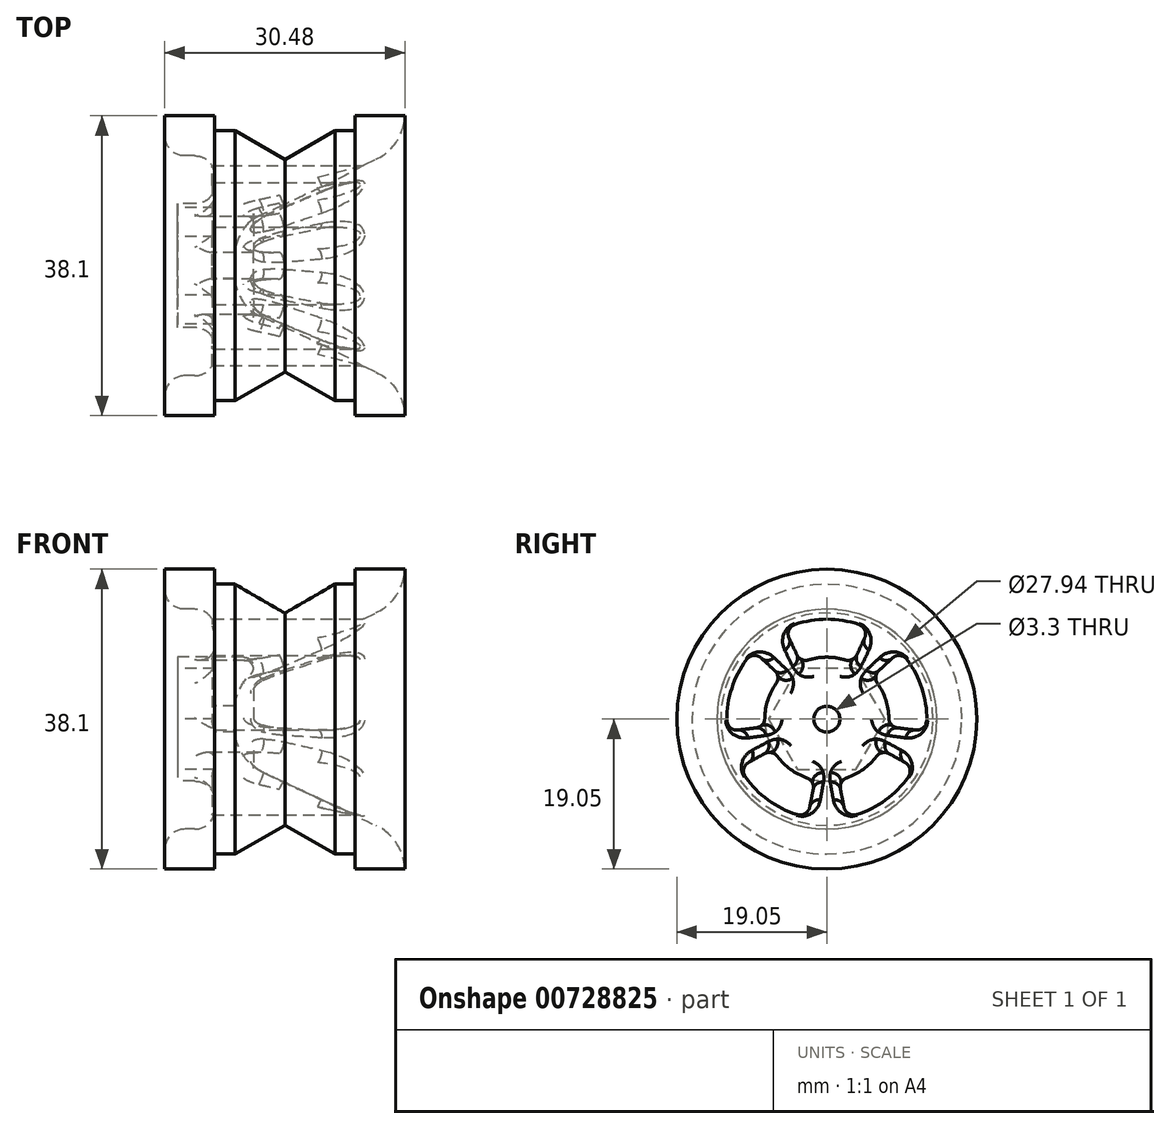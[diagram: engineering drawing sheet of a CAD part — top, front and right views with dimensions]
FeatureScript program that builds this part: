
annotation { "Feature Type Name" : "Feature", "Feature Type Description" : "" }
export const myFeature = defineFeature(function(context is Context, id is Id, definition is map)
    precondition{}
    {
        {
            var Q0;
            Q0=qCreatedBy(makeId("Front.planeOp"),FACE);
            var sketch = newSketch(context, id + "F0", { "sketchPlane" : qUnion([Q0])});
            skLineSegment(sketch, "E0", {"start": v(0, 0) * mm, "end": v(0, 50.34) * mm, "construction": true});
            skLineSegment(sketch, "E1", {"start": v(6.35, 17.15) * mm, "end": v(8.9, 17.15) * mm});
            skLineSegment(sketch, "E2", {"start": v(8.9, 17.15) * mm, "end": v(8.9, 19.05) * mm});
            skLineSegment(sketch, "E3", {"start": v(8.9, 19.05) * mm, "end": v(15.24, 19.05) * mm});
            skLineSegment(sketch, "E4", {"start": v(15.24, 19.05) * mm, "end": v(15.24, 15.24) * mm});
            skLineSegment(sketch, "E5", {"start": v(15.24, 15.24) * mm, "end": v(-6.35, 5.08) * mm});
            skLineSegment(sketch, "E6.MirrorCS", {"start": v(-8.9, 17.15) * mm, "end": v(-8.9, 19.05) * mm});
            skLineSegment(sketch, "E7.MirrorCS", {"start": v(-8.9, 19.05) * mm, "end": v(-15.24, 19.05) * mm});
            skLineSegment(sketch, "E8", {"start": v(-8.9, 7.87) * mm, "end": v(-8.9, 13.97) * mm});
            skLineSegment(sketch, "E9", {"start": v(-8.9, 13.97) * mm, "end": v(-15.24, 13.97) * mm});
            skLineSegment(sketch, "E10", {"start": v(-15.24, 19.05) * mm, "end": v(-15.24, 13.97) * mm});
            skLineSegment(sketch, "E11", {"start": v(-8.9, 7.87) * mm, "end": v(-13.59, 7.87) * mm});
            skLineSegment(sketch, "E12", {"start": v(-13.59, 7.87) * mm, "end": v(-13.59, 0) * mm});
            skLineSegment(sketch, "E13", {"start": v(-27.96, 0) * mm, "end": v(34.54, 0) * mm, "construction": true});
            skLineSegment(sketch, "E14", {"start": v(-6.35, 5.08) * mm, "end": v(-6.35, 0) * mm});
            skLineSegment(sketch, "E15", {"start": v(-13.59, 0) * mm, "end": v(-6.35, 0) * mm});
            skLineSegment(sketch, "E16", {"start": v(-8.9, 17.15) * mm, "end": v(-6.35, 17.15) * mm});
            skLineSegment(sketch, "E17", {"start": v(-6.35, 17.15) * mm, "end": v(0, 13.48) * mm});
            skLineSegment(sketch, "E18", {"start": v(0, 13.48) * mm, "end": v(6.35, 17.15) * mm});
            skSolve(sketch);
        }
        {
            var Q0;
            Q0 = qSketchRegion(id + "F0", true);
            var Q1;
            Q1=sQuery(id+"F0.wireOp",EDGE,"E13");
            revolve(context, id + "F1", {"surfaceOperationType" : NewSurfaceOperationType.NEW, "entities" : qUnion([Q0]), "axis" : qUnion([Q1]), "revolveType" : RevolveType.FULL});
        }
        {
            var Q0;
            Q0=makeQuery(id+"F1.opRevolve","SWEPT_FACE",FACE,{"disambiguationData":[OSD([sQuery(id+"F0.wireOp",EDGE,"E12")])]});
            var sketch = newSketch(context, id + "F2", { "sketchPlane" : qUnion([Q0])});
            skCircle(sketch, "E19.cCircle", {"center": v(0, 0) * mm, "radius": 6.41 * mm, "construction": true});
            skLineSegment(sketch, "E19.0", {"start": v(7.4, 0) * mm, "end": v(3.7, -6.41) * mm});
            skLineSegment(sketch, "E19.1", {"start": v(3.7, -6.41) * mm, "end": v(-3.7, -6.41) * mm});
            skLineSegment(sketch, "E19.2", {"start": v(-3.7, -6.41) * mm, "end": v(-7.4, 0) * mm});
            skLineSegment(sketch, "E19.3", {"start": v(-7.4, 0) * mm, "end": v(-3.7, 6.41) * mm});
            skLineSegment(sketch, "E19.4", {"start": v(-3.7, 6.41) * mm, "end": v(3.7, 6.41) * mm});
            skLineSegment(sketch, "E19.5", {"start": v(3.7, 6.41) * mm, "end": v(7.4, 0) * mm});
            skPoint(sketch, "E19.0.midPoint", {"position": v(5.55, -3.2) * mm});
            skSolve(sketch);
        }
        {
            var Q0;
            Q0 = qSketchRegion(id + "F2", true);
            var Q1;
            Q1=makeQuery(id+"F1.opRevolve","SWEPT_FACE",FACE,{"disambiguationData":[OSD([sQuery(id+"F0.wireOp",EDGE,"E8")])]});
            extrude(context, id + "F3", {"entities" : qUnion([Q0]), "operationType" : NewBodyOperationType.REMOVE, "endBound" : BoundingType.UP_TO_SURFACE, "oppositeDirection" : true, "depth" : 25.4 * mm, "endBoundEntityFace" : qUnion([Q1]), "offsetDistance" : 25.4 * mm});
        }
        {
            var Q0;
            Q0=makeQuery(id+"F3.boolean.opBoolean","COPY",FACE,{"derivedFrom":makeQuery(id+"F3.opExtrude","CAP_FACE",FACE,{"disambiguationData":[OSD([sQuery(id+"F2.wireOp",EDGE,"E19.0"),sQuery(id+"F2.wireOp",EDGE,"E19.1"),sQuery(id+"F2.wireOp",EDGE,"E19.2"),sQuery(id+"F2.wireOp",EDGE,"E19.3"),sQuery(id+"F2.wireOp",EDGE,"E19.4"),sQuery(id+"F2.wireOp",EDGE,"E19.5")])],"isStart":false})});
            var sketch = newSketch(context, id + "F4", { "sketchPlane" : qUnion([Q0])});
            skCircle(sketch, "E20", {"center": v(0, 0) * mm, "radius": 1.65 * mm});
            skSolve(sketch);
        }
        {
            var Q0;
            Q0 = qSketchRegion(id + "F4", true);
            extrude(context, id + "F5", {"entities" : qUnion([Q0]), "operationType" : NewBodyOperationType.REMOVE, "endBound" : BoundingType.THROUGH_ALL, "oppositeDirection" : true, "depth" : 25.4 * mm, "offsetDistance" : 25.4 * mm});
        }
        {
            var Q0;
            Q0=makeQuery(id+"F1.opRevolve","SWEPT_EDGE",EDGE,{"disambiguationData":[OSD([sQuery(id+"F0.wireOp",EDGE,"E5"),sQuery(id+"F0.wireOp",EDGE,"E14")])]});
            var Q1;
            Q1=makeQuery(id+"F1.opRevolve","SWEPT_EDGE",EDGE,{"disambiguationData":[OSD([sQuery(id+"F0.wireOp",EDGE,"E4"),sQuery(id+"F0.wireOp",EDGE,"E5")])]});
            fillet(context, id + "F6", {"entities" : qUnion([Q0, Q1]), "radius" : 6.35 * mm, "tangentPropagation" : true, "allowEdgeOverflow" : false});
        }
        {
            var Q0;
            Q0=makeQuery(id+"F1.opRevolve","SWEPT_EDGE",EDGE,{"disambiguationData":[OSD([sQuery(id+"F0.wireOp",EDGE,"E9"),sQuery(id+"F0.wireOp",EDGE,"E10")])]});
            var Q1;
            Q1=makeQuery(id+"F1.opRevolve","SWEPT_EDGE",EDGE,{"disambiguationData":[OSD([sQuery(id+"F0.wireOp",EDGE,"E8"),sQuery(id+"F0.wireOp",EDGE,"E9")])]});
            var Q2;
            Q2=makeQuery(id+"F1.opRevolve","SWEPT_EDGE",EDGE,{"disambiguationData":[OSD([sQuery(id+"F0.wireOp",EDGE,"E8"),sQuery(id+"F0.wireOp",EDGE,"E11")])]});
            fillet(context, id + "F7", {"entities" : qUnion([Q0, Q1, Q2]), "radius" : 2.54 * mm, "tangentPropagation" : true, "allowEdgeOverflow" : false});
        }
        {
            var Q0;
            Q0=qCreatedBy(makeId("Right.planeOp"),FACE);
            var sketch = newSketch(context, id + "F8", { "sketchPlane" : qUnion([Q0])});
            skLineSegment(sketch, "E21", {"start": v(0, 0) * mm, "end": v(0, 23.07) * mm, "construction": true});
            skArc(sketch, "E22.0", {"start": v(3.33, 7.14) * mm, "mid": v(0, 7.87) * mm, "end": v(-3.33, 7.14) * mm});
            skArc(sketch, "E23", {"start": v(5.37, 11.51) * mm, "mid": v(0, 12.7) * mm, "end": v(-5.37, 11.51) * mm});
            skLineSegment(sketch, "E24", {"start": v(3.33, 7.14) * mm, "end": v(5.37, 11.51) * mm});
            skLineSegment(sketch, "E25.MirrorCS", {"start": v(-3.33, 7.14) * mm, "end": v(-5.37, 11.51) * mm});
            skLineSegment(sketch, "E26.1.0", {"start": v(-7.82, -0.96) * mm, "end": v(-12.6, -1.55) * mm});
            skArc(sketch, "E26.1.1", {"start": v(-9.29, 8.66) * mm, "mid": v(-12.08, 3.92) * mm, "end": v(-12.6, -1.55) * mm});
            skLineSegment(sketch, "E26.1.2", {"start": v(-5.76, 5.37) * mm, "end": v(-9.29, 8.66) * mm});
            skArc(sketch, "E26.1.3", {"start": v(-5.76, 5.37) * mm, "mid": v(-7.49, 2.43) * mm, "end": v(-7.82, -0.96) * mm});
            skLineSegment(sketch, "E26.2.0", {"start": v(-1.5, -7.73) * mm, "end": v(-2.42, -12.47) * mm});
            skArc(sketch, "E26.2.1", {"start": v(-11.1, -6.16) * mm, "mid": v(-7.46, -10.27) * mm, "end": v(-2.42, -12.47) * mm});
            skLineSegment(sketch, "E26.2.2", {"start": v(-6.89, -3.82) * mm, "end": v(-11.1, -6.16) * mm});
            skArc(sketch, "E26.2.3", {"start": v(-6.89, -3.82) * mm, "mid": v(-4.63, -6.37) * mm, "end": v(-1.5, -7.73) * mm});
            skLineSegment(sketch, "E26.3.0", {"start": v(6.89, -3.82) * mm, "end": v(11.1, -6.16) * mm});
            skArc(sketch, "E26.3.1", {"start": v(2.42, -12.47) * mm, "mid": v(7.46, -10.27) * mm, "end": v(11.1, -6.16) * mm});
            skLineSegment(sketch, "E26.3.2", {"start": v(1.5, -7.73) * mm, "end": v(2.42, -12.47) * mm});
            skArc(sketch, "E26.3.3", {"start": v(1.5, -7.73) * mm, "mid": v(4.63, -6.37) * mm, "end": v(6.89, -3.82) * mm});
            skLineSegment(sketch, "E26.4.0", {"start": v(5.76, 5.37) * mm, "end": v(9.29, 8.66) * mm});
            skArc(sketch, "E26.4.1", {"start": v(12.6, -1.55) * mm, "mid": v(12.08, 3.92) * mm, "end": v(9.29, 8.66) * mm});
            skLineSegment(sketch, "E26.4.2", {"start": v(7.82, -0.96) * mm, "end": v(12.6, -1.55) * mm});
            skArc(sketch, "E26.4.3", {"start": v(7.82, -0.96) * mm, "mid": v(7.49, 2.43) * mm, "end": v(5.76, 5.37) * mm});
            skSolve(sketch);
        }
        {
            var Q0;
            Q0 = qSketchRegion(id + "F8", true);
            extrude(context, id + "F9", {"entities" : qUnion([Q0]), "operationType" : NewBodyOperationType.REMOVE, "endBound" : BoundingType.THROUGH_ALL, "oppositeDirection" : true, "depth" : 25.4 * mm, "offsetDistance" : 25.4 * mm, "hasSecondDirection" : true, "secondDirectionBound" : SecondDirectionBoundingType.THROUGH_ALL, "secondDirectionOppositeDirection" : false, "secondDirectionDepth" : 25.4 * mm});
        }
        {
            var Q0;
            Q0=makeQuery(id+"F9.boolean.opBoolean","COPY",EDGE,{"derivedFrom":makeQuery(id+"F9.opExtrude","SWEPT_EDGE",EDGE,{"disambiguationData":[OSD([sQuery(id+"F8.wireOp",EDGE,"E23"),sQuery(id+"F8.wireOp",EDGE,"E24")])]})});
            var Q1;
            Q1=makeQuery(id+"F9.boolean.opBoolean","COPY",EDGE,{"derivedFrom":makeQuery(id+"F9.opExtrude","SWEPT_EDGE",EDGE,{"disambiguationData":[OSD([sQuery(id+"F8.wireOp",EDGE,"E23"),sQuery(id+"F8.wireOp",EDGE,"E25.MirrorCS")])]})});
            var Q2;
            Q2=makeQuery(id+"F9.boolean.opBoolean","COPY",EDGE,{"derivedFrom":makeQuery(id+"F9.opExtrude","SWEPT_EDGE",EDGE,{"disambiguationData":[OSD([sQuery(id+"F8.wireOp",EDGE,"E22.0"),sQuery(id+"F8.wireOp",EDGE,"E25.MirrorCS")])]})});
            var Q3;
            Q3=makeQuery(id+"F9.boolean.opBoolean","COPY",EDGE,{"derivedFrom":makeQuery(id+"F9.opExtrude","SWEPT_EDGE",EDGE,{"disambiguationData":[OSD([sQuery(id+"F8.wireOp",EDGE,"E22.0"),sQuery(id+"F8.wireOp",EDGE,"E24")])]})});
            var Q4;
            Q4=makeQuery(id+"F9.boolean.opBoolean","COPY",EDGE,{"derivedFrom":makeQuery(id+"F9.opExtrude","SWEPT_EDGE",EDGE,{"disambiguationData":[OSD([sQuery(id+"F8.wireOp",EDGE,"E26.1.2"),sQuery(id+"F8.wireOp",EDGE,"E26.1.3")])]})});
            var Q5;
            Q5=makeQuery(id+"F9.boolean.opBoolean","COPY",EDGE,{"derivedFrom":makeQuery(id+"F9.opExtrude","SWEPT_EDGE",EDGE,{"disambiguationData":[OSD([sQuery(id+"F8.wireOp",EDGE,"E26.1.1"),sQuery(id+"F8.wireOp",EDGE,"E26.1.2")])]})});
            var Q6;
            Q6=makeQuery(id+"F9.boolean.opBoolean","COPY",EDGE,{"derivedFrom":makeQuery(id+"F9.opExtrude","SWEPT_EDGE",EDGE,{"disambiguationData":[OSD([sQuery(id+"F8.wireOp",EDGE,"E26.1.0"),sQuery(id+"F8.wireOp",EDGE,"E26.1.1")])]})});
            var Q7;
            Q7=makeQuery(id+"F9.boolean.opBoolean","COPY",EDGE,{"derivedFrom":makeQuery(id+"F9.opExtrude","SWEPT_EDGE",EDGE,{"disambiguationData":[OSD([sQuery(id+"F8.wireOp",EDGE,"E26.1.0"),sQuery(id+"F8.wireOp",EDGE,"E26.1.3")])]})});
            var Q8;
            Q8=makeQuery(id+"F9.boolean.opBoolean","COPY",EDGE,{"derivedFrom":makeQuery(id+"F9.opExtrude","SWEPT_EDGE",EDGE,{"disambiguationData":[OSD([sQuery(id+"F8.wireOp",EDGE,"E26.2.0"),sQuery(id+"F8.wireOp",EDGE,"E26.2.3")])]})});
            var Q9;
            Q9=makeQuery(id+"F9.boolean.opBoolean","COPY",EDGE,{"derivedFrom":makeQuery(id+"F9.opExtrude","SWEPT_EDGE",EDGE,{"disambiguationData":[OSD([sQuery(id+"F8.wireOp",EDGE,"E26.2.0"),sQuery(id+"F8.wireOp",EDGE,"E26.2.1")])]})});
            var Q10;
            Q10=makeQuery(id+"F9.boolean.opBoolean","COPY",EDGE,{"derivedFrom":makeQuery(id+"F9.opExtrude","SWEPT_EDGE",EDGE,{"disambiguationData":[OSD([sQuery(id+"F8.wireOp",EDGE,"E26.2.2"),sQuery(id+"F8.wireOp",EDGE,"E26.2.3")])]})});
            var Q11;
            Q11=makeQuery(id+"F9.boolean.opBoolean","COPY",EDGE,{"derivedFrom":makeQuery(id+"F9.opExtrude","SWEPT_EDGE",EDGE,{"disambiguationData":[OSD([sQuery(id+"F8.wireOp",EDGE,"E26.2.1"),sQuery(id+"F8.wireOp",EDGE,"E26.2.2")])]})});
            var Q12;
            Q12=makeQuery(id+"F9.boolean.opBoolean","COPY",EDGE,{"derivedFrom":makeQuery(id+"F9.opExtrude","SWEPT_EDGE",EDGE,{"disambiguationData":[OSD([sQuery(id+"F8.wireOp",EDGE,"E26.3.1"),sQuery(id+"F8.wireOp",EDGE,"E26.3.2")])]})});
            var Q13;
            Q13=makeQuery(id+"F9.boolean.opBoolean","COPY",EDGE,{"derivedFrom":makeQuery(id+"F9.opExtrude","SWEPT_EDGE",EDGE,{"disambiguationData":[OSD([sQuery(id+"F8.wireOp",EDGE,"E26.3.2"),sQuery(id+"F8.wireOp",EDGE,"E26.3.3")])]})});
            var Q14;
            Q14=makeQuery(id+"F9.boolean.opBoolean","COPY",EDGE,{"derivedFrom":makeQuery(id+"F9.opExtrude","SWEPT_EDGE",EDGE,{"disambiguationData":[OSD([sQuery(id+"F8.wireOp",EDGE,"E26.3.0"),sQuery(id+"F8.wireOp",EDGE,"E26.3.3")])]})});
            var Q15;
            Q15=makeQuery(id+"F9.boolean.opBoolean","COPY",EDGE,{"derivedFrom":makeQuery(id+"F9.opExtrude","SWEPT_EDGE",EDGE,{"disambiguationData":[OSD([sQuery(id+"F8.wireOp",EDGE,"E26.3.0"),sQuery(id+"F8.wireOp",EDGE,"E26.3.1")])]})});
            var Q16;
            Q16=makeQuery(id+"F9.boolean.opBoolean","COPY",EDGE,{"derivedFrom":makeQuery(id+"F9.opExtrude","SWEPT_EDGE",EDGE,{"disambiguationData":[OSD([sQuery(id+"F8.wireOp",EDGE,"E26.4.1"),sQuery(id+"F8.wireOp",EDGE,"E26.4.2")])]})});
            var Q17;
            Q17=makeQuery(id+"F9.boolean.opBoolean","COPY",EDGE,{"derivedFrom":makeQuery(id+"F9.opExtrude","SWEPT_EDGE",EDGE,{"disambiguationData":[OSD([sQuery(id+"F8.wireOp",EDGE,"E26.4.2"),sQuery(id+"F8.wireOp",EDGE,"E26.4.3")])]})});
            var Q18;
            Q18=makeQuery(id+"F9.boolean.opBoolean","COPY",EDGE,{"derivedFrom":makeQuery(id+"F9.opExtrude","SWEPT_EDGE",EDGE,{"disambiguationData":[OSD([sQuery(id+"F8.wireOp",EDGE,"E26.4.0"),sQuery(id+"F8.wireOp",EDGE,"E26.4.3")])]})});
            var Q19;
            Q19=makeQuery(id+"F9.boolean.opBoolean","COPY",EDGE,{"derivedFrom":makeQuery(id+"F9.opExtrude","SWEPT_EDGE",EDGE,{"disambiguationData":[OSD([sQuery(id+"F8.wireOp",EDGE,"E26.4.0"),sQuery(id+"F8.wireOp",EDGE,"E26.4.1")])]})});
            fillet(context, id + "F10", {"entities" : qUnion([Q0, Q1, Q2, Q3, Q4, Q5, Q6, Q7, Q8, Q9, Q10, Q11, Q12, Q13, Q14, Q15, Q16, Q17, Q18, Q19]), "radius" : 1.27 * mm, "tangentPropagation" : true, "allowEdgeOverflow" : false});
        }
        {
            var Q0;
            Q0=makeQuery(id+"F9.boolean.opBoolean","INTERSECT",EDGE,{"derivedFrom":[makeQuery(id+"F1.opRevolve","SWEPT_FACE",FACE,{"disambiguationData":[OSD([sQuery(id+"F0.wireOp",EDGE,"E5")])]}),makeQuery(id+"F9.opExtrude","SWEPT_FACE",FACE,{"disambiguationData":[OSD([sQuery(id+"F8.wireOp",EDGE,"E26.2.1")])]})]});
            var Q1;
            Q1=makeQuery(id+"F9.boolean.opBoolean","INTERSECT",EDGE,{"derivedFrom":[makeQuery(id+"F1.opRevolve","SWEPT_FACE",FACE,{"disambiguationData":[OSD([sQuery(id+"F0.wireOp",EDGE,"E5")])]}),makeQuery(id+"F9.opExtrude","SWEPT_FACE",FACE,{"disambiguationData":[OSD([sQuery(id+"F8.wireOp",EDGE,"E26.1.1")])]})]});
            var Q2;
            Q2=makeQuery(id+"F9.boolean.opBoolean","INTERSECT",EDGE,{"derivedFrom":[makeQuery(id+"F1.opRevolve","SWEPT_FACE",FACE,{"disambiguationData":[OSD([sQuery(id+"F0.wireOp",EDGE,"E5")])]}),makeQuery(id+"F9.opExtrude","SWEPT_FACE",FACE,{"disambiguationData":[OSD([sQuery(id+"F8.wireOp",EDGE,"E23")])]})]});
            var Q3;
            Q3=makeQuery(id+"F9.boolean.opBoolean","INTERSECT",EDGE,{"derivedFrom":[makeQuery(id+"F1.opRevolve","SWEPT_FACE",FACE,{"disambiguationData":[OSD([sQuery(id+"F0.wireOp",EDGE,"E5")])]}),makeQuery(id+"F9.opExtrude","SWEPT_FACE",FACE,{"disambiguationData":[OSD([sQuery(id+"F8.wireOp",EDGE,"E26.4.1")])]})]});
            var Q4;
            Q4=makeQuery(id+"F9.boolean.opBoolean","INTERSECT",EDGE,{"derivedFrom":[makeQuery(id+"F1.opRevolve","SWEPT_FACE",FACE,{"disambiguationData":[OSD([sQuery(id+"F0.wireOp",EDGE,"E5")])]}),makeQuery(id+"F9.opExtrude","SWEPT_FACE",FACE,{"disambiguationData":[OSD([sQuery(id+"F8.wireOp",EDGE,"E26.3.1")])]})]});
            fillet(context, id + "F11", {"entities" : qUnion([Q0, Q1, Q2, Q3, Q4]), "radius" : 1.27 * mm, "tangentPropagation" : true, "allowEdgeOverflow" : false});
        }
    });
